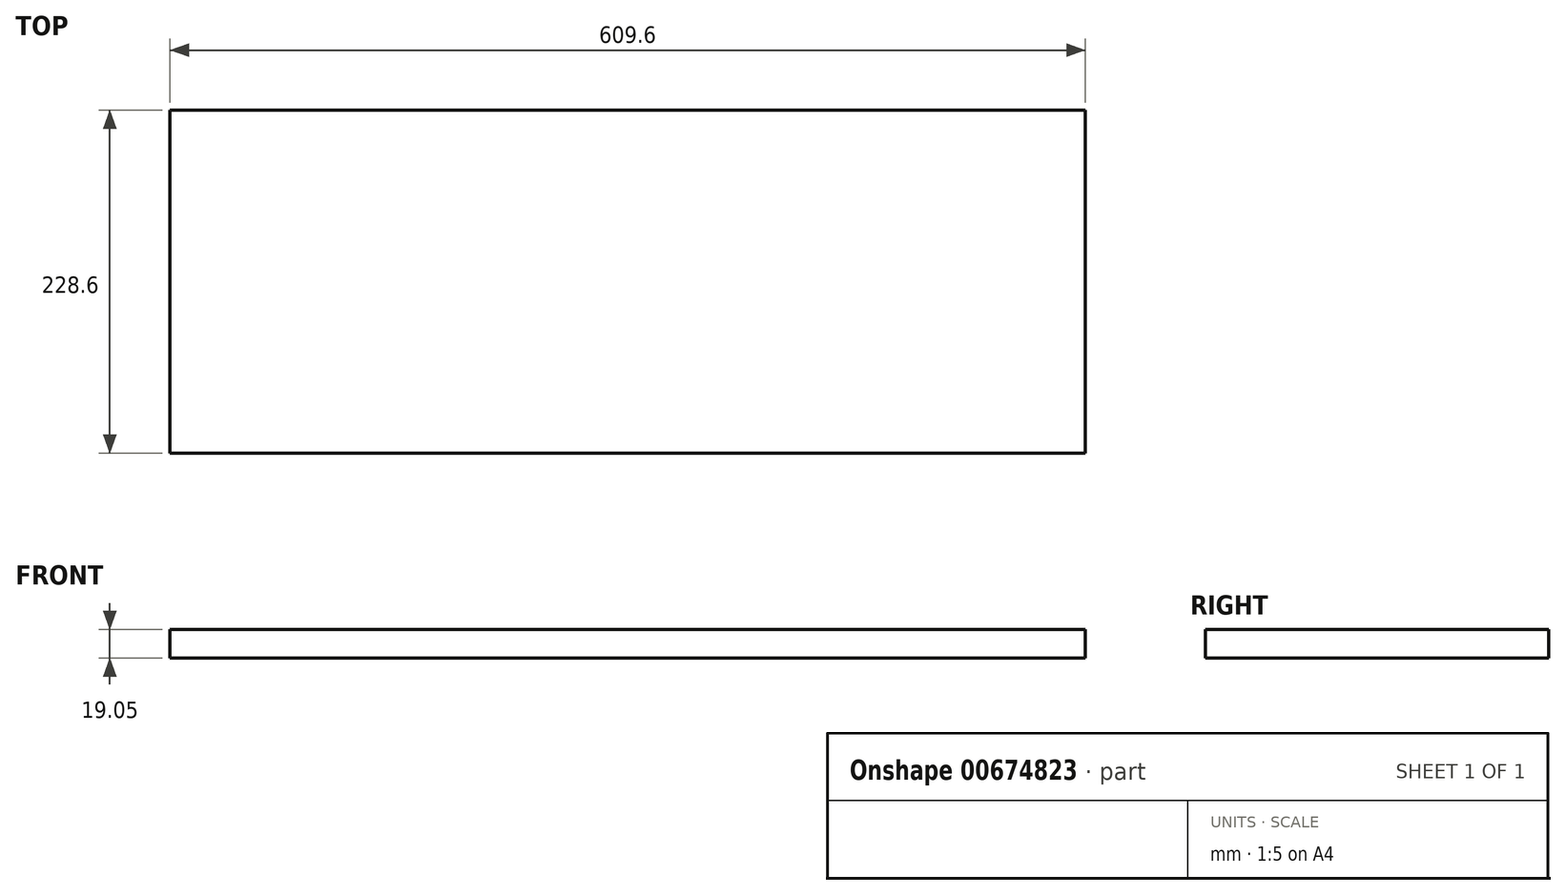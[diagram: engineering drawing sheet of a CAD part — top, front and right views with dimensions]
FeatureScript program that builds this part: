
annotation { "Feature Type Name" : "Feature", "Feature Type Description" : "" }
export const myFeature = defineFeature(function(context is Context, id is Id, definition is map)
    precondition{}
    {
        {
            var Q0;
            Q0=qCreatedBy(makeId("Top.planeOp"),FACE);
            var sketch = newSketch(context, id + "F0", { "sketchPlane" : qUnion([Q0])});
            skLineSegment(sketch, "E0.bottom", {"start": v(-304.8, 114.3) * mm, "end": v(304.8, 114.3) * mm});
            skLineSegment(sketch, "E0.top", {"start": v(-304.8, -114.3) * mm, "end": v(304.8, -114.3) * mm});
            skLineSegment(sketch, "E0.left", {"start": v(-304.8, 114.3) * mm, "end": v(-304.8, -114.3) * mm});
            skLineSegment(sketch, "E0.right", {"start": v(304.8, 114.3) * mm, "end": v(304.8, -114.3) * mm});
            skPoint(sketch, "E0.middle", {"position": v(0, 0) * mm});
            skSolve(sketch);
        }
        {
            var Q0;
            Q0=makeQuery(id+"F0.imprint","IMPRINT",FACE,{"disambiguationData":[TD([[makeQuery(id+"F0.imprint","IMPRINT",EDGE,{"derivedFrom":sQuery(id+"F0.wireOp",EDGE,"E0.bottom")}),-1.0]])]});
            extrude(context, id + "F1", {"entities" : qUnion([Q0]), "depth" : 19.05 * mm, "offsetDistance" : 25.4 * mm});
        }
    });
